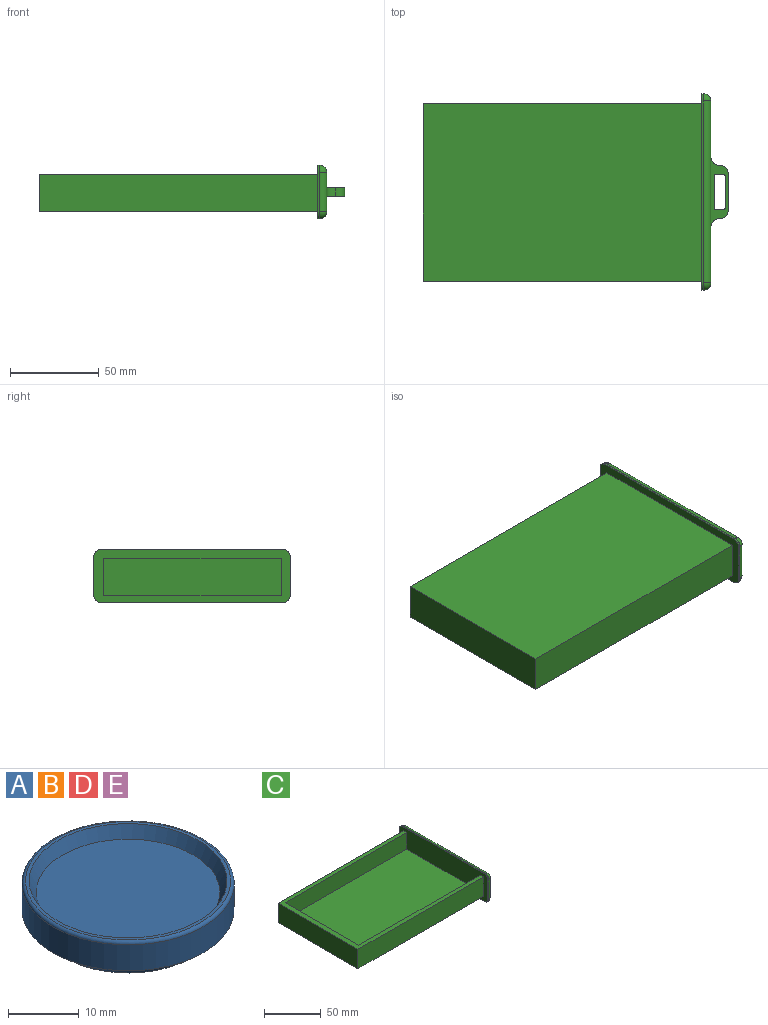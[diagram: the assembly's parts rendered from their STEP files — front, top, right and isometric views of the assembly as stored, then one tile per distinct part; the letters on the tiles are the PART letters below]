
ASSEMBLY  parts=5 mates=1
PART A: 8 faces, bbox 32.5x32.5x7 mm
  f0: cone r=13mm half-angle=26.6deg, axis (0,0,1), area 189.7mm2, adj f1,f7
  f1: plane 26x26mm, normal (0,0,1), area 530.9mm2, adj f0
  f2: plane 25.4x25.4mm, normal (0,0,-1), area 506.7mm2, adj f3
  f3: cone r=12.7mm half-angle=24.2deg, axis (0,0,1), area 181.2mm2, adj f2,f4
  f4: plane 30x30mm, normal (0,0,-1), area 125.8mm2, adj f3,f5
  f5: cylinder r=15mm len=30mm, axis (0,0,1), area 424.1mm2, adj f4,f6
  f6: torus R=14.5mm, axis (0,0,1), area 73.1mm2, adj f5,f7
  f7: plane 29x29mm, normal (0,0,1), area 44.8mm2, adj f0,f6
PART B: same geometry as A
PART C: 42 faces, bbox 172x110.5x30 mm
  f0: plane 110.54x30mm, normal (-1,0,0), area 2858.6mm2, adj f1,f2,f3,f4,f5,f6,f8,f9
  f1: plane 157x21mm, normal (0,-1,0), area 3297mm2, adj f0,f3,f4,f41
  f2: plane 152x18mm, normal (0,1,0), area 2736mm2, adj f0,f3,f12,f40
  f3: plane 157x100mm, normal (0,0,1), area 1716mm2, adj f0,f1,f2,f5,f6,f40,f41
  f4: plane 157x100mm, normal (0,0,-1), area 15700mm2, adj f0,f1,f5,f41
  f5: plane 157x21mm, normal (0,1,0), area 3297mm2, adj f0,f3,f4,f41
  f6: plane 152x18mm, normal (0,-1,0), area 2736mm2, adj f0,f3,f12,f40
  f7: plane 102.54x22mm, normal (1,0,0), area 2056mm2, adj f14,f19,f20,f24,f25,f26,f37,f39
  f8: plane 22x1mm, normal (0,1,0), area 22mm2, adj f0,f13,f14,f15
  f9: plane 22x1mm, normal (0,-1,0), area 22mm2, adj f0,f18,f21,f24
  f10: plane 102.54x1mm, normal (0,0,1), area 102.5mm2, adj f0,f13,f18,f19
  f11: plane 102.54x1mm, normal (0,0,-1), area 102.5mm2, adj f0,f15,f20,f21
  f12: plane 152x92mm, normal (0,0,1), area 13984mm2, adj f0,f2,f6,f40
  f13: cylinder r=4mm len=4mm, axis (1,0,0), area 6.3mm2, adj f0,f8,f10,f16
  f14: cylinder r=4mm len=22mm, axis (0,0,1), area 138.2mm2, adj f7,f8,f16,f17
  f15: cylinder r=4mm len=4mm, axis (-1,0,0), area 6.3mm2, adj f0,f8,f11,f17
  f16: sphere r=4mm, area 25.1mm2, adj f13,f14,f19
  f17: sphere r=4mm, area 25.1mm2, adj f14,f15,f20
  f18: cylinder r=4mm len=4mm, axis (-1,0,0), area 6.3mm2, adj f0,f9,f10,f22
  f19: cylinder r=4mm len=102.54mm, axis (0,-1,0), area 644.3mm2, adj f7,f10,f16,f22
  f20: cylinder r=4mm len=102.54mm, axis (0,1,0), area 644.3mm2, adj f7,f11,f17,f23
  f21: cylinder r=4mm len=4mm, axis (1,0,0), area 6.3mm2, adj f0,f9,f11,f23
  f22: sphere r=4mm, area 25.1mm2, adj f18,f19,f24
  f23: sphere r=4mm, area 25.1mm2, adj f20,f21,f24
  f24: cylinder r=4mm len=22mm, axis (0,0,-1), area 138.2mm2, adj f7,f9,f22,f23
  f25: plane 40x10mm, normal (0,0,1), area 180.9mm2, adj f7,f27,f28,f29,f30,f31,f32,f33
  f26: plane 40x10mm, normal (0,0,-1), area 180.9mm2, adj f7,f27,f28,f29,f30,f31,f32,f33
  f27: plane 20x5mm, normal (1,0,0), area 100mm2, adj f25,f26,f36,f38
  f28: plane 5x4mm, normal (0,1,0), area 20mm2, adj f25,f26,f29,f35
  f29: cylinder r=1mm len=5mm, axis (0,0,1), area 7.9mm2, adj f25,f26,f28,f30
  f30: plane 18x5mm, normal (-1,0,0), area 90mm2, adj f25,f26,f29,f31
  f31: cylinder r=1mm len=5mm, axis (0,0,1), area 7.9mm2, adj f25,f26,f30,f32
  f32: plane 5x4mm, normal (0,-1,0), area 20mm2, adj f25,f26,f31,f33
  f33: cylinder r=1mm len=5mm, axis (0,0,1), area 7.9mm2, adj f25,f26,f32,f34
  f34: plane 18x5mm, normal (1,0,0), area 90mm2, adj f25,f26,f33,f35
  f35: cylinder r=1mm len=5mm, axis (0,0,1), area 7.9mm2, adj f25,f26,f28,f34
  f36: cylinder r=5mm len=5mm, axis (0,0,1), area 39.3mm2, adj f25,f26,f27,f37
  f37: cylinder r=5mm len=5mm, axis (0,0,1), area 39.3mm2, adj f7,f25,f26,f36
  f38: cylinder r=5mm len=5mm, axis (0,0,-1), area 39.3mm2, adj f25,f26,f27,f39
  f39: cylinder r=5mm len=5mm, axis (0,0,-1), area 39.3mm2, adj f7,f25,f26,f38
  f40: plane 92x18mm, normal (1,0,0), area 1656mm2, adj f2,f3,f6,f12
  f41: plane 100x21mm, normal (-1,0,0), area 2100mm2, adj f1,f3,f4,f5
PART D: same geometry as A
PART E: same geometry as A
PLACE A t=(-33.38,20.48,36.72)mm
PLACE B t=(26.62,20.48,36.72)mm
PLACE C rot(axis=(1,0,0),180deg) t=(-113.38,100.48,46.22)mm
PLACE D t=(-2.38,21.48,36.72)mm
PLACE E t=(-93.38,20.48,36.72)mm
MATE fastened E.f0 <-> C.f12  axis (0,0,1) through (-93.38,20.48,43.22)mm
